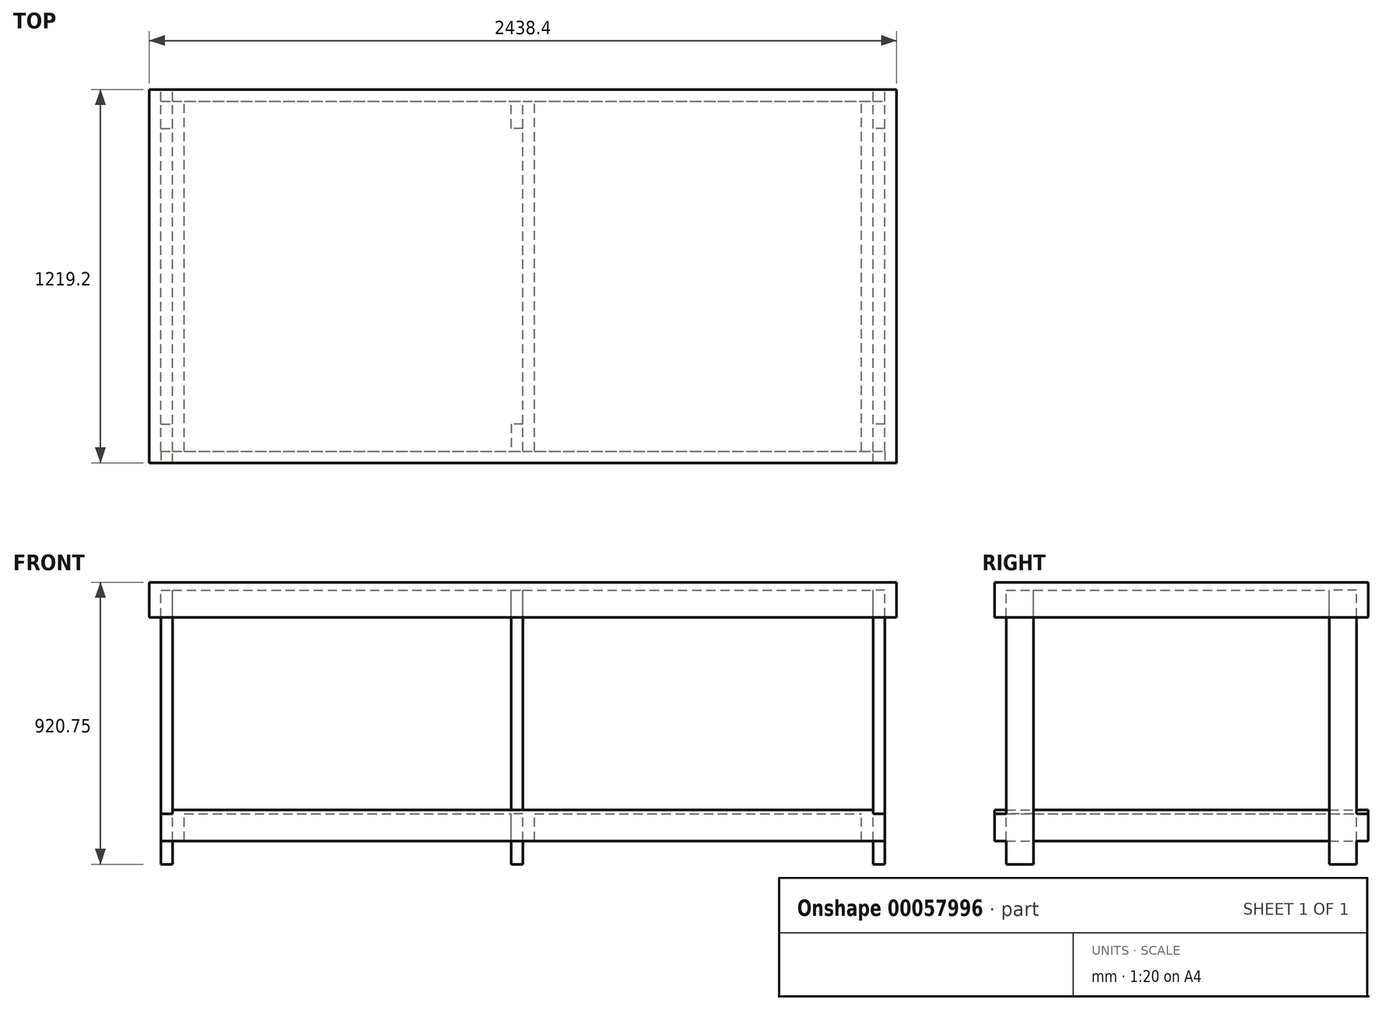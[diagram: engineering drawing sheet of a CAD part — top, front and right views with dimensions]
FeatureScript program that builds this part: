
annotation { "Feature Type Name" : "Feature", "Feature Type Description" : "" }
export const myFeature = defineFeature(function(context is Context, id is Id, definition is map)
    precondition{}
    {
        {
            var Q0;
            Q0=qCreatedBy(makeId("Top.planeOp"),FACE);
            var sketch = newSketch(context, id + "F0", { "sketchPlane" : qUnion([Q0])});
            skLineSegment(sketch, "E0.bottom", {"start": v(0, 0) * mm, "end": v(2438.4, 0) * mm});
            skLineSegment(sketch, "E0.top", {"start": v(0, -1219.2) * mm, "end": v(2438.4, -1219.2) * mm});
            skLineSegment(sketch, "E0.left", {"start": v(0, 0) * mm, "end": v(0, -1219.2) * mm});
            skLineSegment(sketch, "E0.right", {"start": v(2438.4, 0) * mm, "end": v(2438.4, -1219.2) * mm});
            skSolve(sketch);
        }
        {
            var Q0;
            Q0 = qSketchRegion(id + "F0", true);
            extrude(context, id + "F1", {"entities" : qUnion([Q0]), "depth" : 25.4 * mm});
        }
        {
            var Q0;
            Q0=makeQuery(id+"F1.opExtrude","CAP_FACE",FACE,{"disambiguationData":[OSD([sQuery(id+"F0.wireOp",EDGE,"E0.bottom"),sQuery(id+"F0.wireOp",EDGE,"E0.top"),sQuery(id+"F0.wireOp",EDGE,"E0.left"),sQuery(id+"F0.wireOp",EDGE,"E0.right")])],"isStart":true});
            var sketch = newSketch(context, id + "F2", { "sketchPlane" : qUnion([Q0])});
            skLineSegment(sketch, "E1.bottom", {"start": v(0, 1219.2) * mm, "end": v(2438.4, 1219.2) * mm});
            skLineSegment(sketch, "E1.top", {"start": v(0, 0) * mm, "end": v(2438.4, 0) * mm});
            skLineSegment(sketch, "E1.left", {"start": v(0, 1219.2) * mm, "end": v(0, 0) * mm});
            skLineSegment(sketch, "E1.right", {"start": v(2438.4, 1219.2) * mm, "end": v(2438.4, 0) * mm});
            skLineSegment(sketch, "E2.0", {"start": v(38.1, 1181.1) * mm, "end": v(2400.3, 1181.1) * mm});
            skLineSegment(sketch, "E2.1", {"start": v(38.1, 1181.1) * mm, "end": v(38.1, 38.1) * mm});
            skLineSegment(sketch, "E2.2", {"start": v(38.1, 38.1) * mm, "end": v(2400.3, 38.1) * mm});
            skLineSegment(sketch, "E2.3", {"start": v(2400.3, 1181.1) * mm, "end": v(2400.3, 38.1) * mm});
            skSolve(sketch);
        }
        {
            var Q0;
            Q0 = qSketchRegion(id + "F2", true);
            extrude(context, id + "F3", {"entities" : qUnion([Q0]), "operationType" : NewBodyOperationType.ADD, "depth" : 88.9 * mm});
        }
        {
            var Q0;
            Q0=makeQuery(id+"F1.opExtrude","CAP_FACE",FACE,{"disambiguationData":[OSD([sQuery(id+"F0.wireOp",EDGE,"E0.bottom"),sQuery(id+"F0.wireOp",EDGE,"E0.top"),sQuery(id+"F0.wireOp",EDGE,"E0.left"),sQuery(id+"F0.wireOp",EDGE,"E0.right")])],"isStart":true});
            var sketch = newSketch(context, id + "F4", { "sketchPlane" : qUnion([Q0])});
            skLineSegment(sketch, "E3.bottom", {"start": v(38.1, 1181.1) * mm, "end": v(76.2, 1181.1) * mm});
            skLineSegment(sketch, "E3.top", {"start": v(38.1, 1092.2) * mm, "end": v(76.2, 1092.2) * mm});
            skLineSegment(sketch, "E3.left", {"start": v(38.1, 1181.1) * mm, "end": v(38.1, 1092.2) * mm});
            skLineSegment(sketch, "E3.right", {"start": v(76.2, 1181.1) * mm, "end": v(76.2, 1092.2) * mm});
            skLineSegment(sketch, "E4.bottom", {"start": v(38.1, 38.1) * mm, "end": v(76.2, 38.1) * mm});
            skLineSegment(sketch, "E4.top", {"start": v(38.1, 127) * mm, "end": v(76.2, 127) * mm});
            skLineSegment(sketch, "E4.left", {"start": v(38.1, 38.1) * mm, "end": v(38.1, 127) * mm});
            skLineSegment(sketch, "E4.right", {"start": v(76.2, 38.1) * mm, "end": v(76.2, 127) * mm});
            skLineSegment(sketch, "E5.bottom", {"start": v(2400.3, 1181.1) * mm, "end": v(2362.2, 1181.1) * mm});
            skLineSegment(sketch, "E5.top", {"start": v(2400.3, 1092.2) * mm, "end": v(2362.2, 1092.2) * mm});
            skLineSegment(sketch, "E5.left", {"start": v(2400.3, 1181.1) * mm, "end": v(2400.3, 1092.2) * mm});
            skLineSegment(sketch, "E5.right", {"start": v(2362.2, 1181.1) * mm, "end": v(2362.2, 1092.2) * mm});
            skLineSegment(sketch, "E6.bottom", {"start": v(2400.3, 38.1) * mm, "end": v(2362.2, 38.1) * mm});
            skLineSegment(sketch, "E6.top", {"start": v(2400.3, 127) * mm, "end": v(2362.2, 127) * mm});
            skLineSegment(sketch, "E6.left", {"start": v(2400.3, 38.1) * mm, "end": v(2400.3, 127) * mm});
            skLineSegment(sketch, "E6.right", {"start": v(2362.2, 38.1) * mm, "end": v(2362.2, 127) * mm});
            skLineSegment(sketch, "E7.bottom", {"start": v(1181.1, 1181.1) * mm, "end": v(1219.2, 1181.1) * mm});
            skLineSegment(sketch, "E7.top", {"start": v(1181.1, 1092.2) * mm, "end": v(1219.2, 1092.2) * mm});
            skLineSegment(sketch, "E7.left", {"start": v(1181.1, 1181.1) * mm, "end": v(1181.1, 1092.2) * mm});
            skLineSegment(sketch, "E7.right", {"start": v(1219.2, 1181.1) * mm, "end": v(1219.2, 1092.2) * mm});
            skLineSegment(sketch, "E8.bottom", {"start": v(1181.1, 38.1) * mm, "end": v(1219.2, 38.1) * mm});
            skLineSegment(sketch, "E8.top", {"start": v(1181.1, 127) * mm, "end": v(1219.2, 127) * mm});
            skLineSegment(sketch, "E8.left", {"start": v(1181.1, 38.1) * mm, "end": v(1181.1, 127) * mm});
            skLineSegment(sketch, "E8.right", {"start": v(1219.2, 38.1) * mm, "end": v(1219.2, 127) * mm});
            skSolve(sketch);
        }
        {
            var Q0;
            Q0 = qSketchRegion(id + "F4", true);
            extrude(context, id + "F5", {"entities" : qUnion([Q0]), "operationType" : NewBodyOperationType.ADD, "depth" : 895.35 * mm});
        }
        {
            var Q0;
            Q0=qCreatedBy(makeId("Top.planeOp"),FACE);
            cPlane(context, id + "F6", {"entities" : qUnion([Q0]), "cplaneType" : CPlaneType.OFFSET, "offset" : 730.25 * mm, "oppositeDirection" : true, "width" : 152.4 * mm, "height" : 152.4 * mm});
        }
        {
            var Q0;
            Q0=qCreatedBy(id+"F6.planeOp",FACE);
            var sketch = newSketch(context, id + "F7", { "sketchPlane" : qUnion([Q0])});
            skLineSegment(sketch, "E9.bottom", {"start": v(38.1, 0) * mm, "end": v(2400.3, 0) * mm});
            skLineSegment(sketch, "E10.bottom", {"start": v(38.1, -1219.2) * mm, "end": v(2400.3, -1219.2) * mm});
            skLineSegment(sketch, "E10.top", {"start": v(38.1, -1181.1) * mm, "end": v(76.2, -1181.1) * mm});
            skLineSegment(sketch, "E11.right", {"start": v(2324.1, -1181.1) * mm, "end": v(2324.1, -38.1) * mm});
            skLineSegment(sketch, "E12.left", {"start": v(76.2, -1181.1) * mm, "end": v(76.2, -38.1) * mm});
            skLineSegment(sketch, "E12.right", {"start": v(114.3, -1181.1) * mm, "end": v(114.3, -38.1) * mm});
            skLineSegment(sketch, "E13.left", {"start": v(1219.2, -1181.1) * mm, "end": v(1219.2, -38.1) * mm});
            skLineSegment(sketch, "E13.right", {"start": v(1257.3, -1181.1) * mm, "end": v(1257.3, -38.1) * mm});
            skLineSegment(sketch, "E14.trimOffspring", {"start": v(114.3, -38.1) * mm, "end": v(1219.2, -38.1) * mm});
            skLineSegment(sketch, "E15.trimOffspring", {"start": v(114.3, -1181.1) * mm, "end": v(1219.2, -1181.1) * mm});
            skLineSegment(sketch, "E16.trimOffspring", {"start": v(1257.3, -1181.1) * mm, "end": v(2324.1, -1181.1) * mm});
            skLineSegment(sketch, "E17.trimOffspring", {"start": v(1257.3, -38.1) * mm, "end": v(2324.1, -38.1) * mm});
            skLineSegment(sketch, "E18.trimOffspring", {"start": v(2362.2, -38.1) * mm, "end": v(2400.3, -38.1) * mm});
            skLineSegment(sketch, "E19.trimOffspring", {"start": v(2362.2, -1181.1) * mm, "end": v(2400.3, -1181.1) * mm});
            skLineSegment(sketch, "E20", {"start": v(38.1, -1181.1) * mm, "end": v(38.1, -1219.2) * mm});
            skPoint(sketch, "E21.orphan", {"position": v(0, -1219.2) * mm});
            skPoint(sketch, "E22.orphan", {"position": v(0, -1181.1) * mm});
            skLineSegment(sketch, "E23", {"start": v(38.1, -38.1) * mm, "end": v(38.1, 0) * mm});
            skLineSegment(sketch, "E24", {"start": v(2400.3, -1181.1) * mm, "end": v(2400.3, -1219.2) * mm});
            skLineSegment(sketch, "E25", {"start": v(2400.3, -38.1) * mm, "end": v(2400.3, 0) * mm});
            skLineSegment(sketch, "E26", {"start": v(38.1, -38.1) * mm, "end": v(76.2, -38.1) * mm});
            skLineSegment(sketch, "E27", {"start": v(2362.2, -1181.1) * mm, "end": v(2362.2, -38.1) * mm});
            skSolve(sketch);
        }
        {
            var Q0;
            Q0 = qSketchRegion(id + "F7", true);
            extrude(context, id + "F8", {"entities" : qUnion([Q0]), "operationType" : NewBodyOperationType.ADD, "oppositeDirection" : true, "depth" : 88.9 * mm});
        }
        {
            var Q0;
            Q0=qCreatedBy(id+"F6.planeOp",FACE);
            var sketch = newSketch(context, id + "F9", { "sketchPlane" : qUnion([Q0])});
            skLineSegment(sketch, "E28.bottom", {"start": v(76.2, -1219.2) * mm, "end": v(2362.2, -1219.2) * mm});
            skLineSegment(sketch, "E28.top", {"start": v(76.2, 0) * mm, "end": v(2362.2, 0) * mm});
            skLineSegment(sketch, "E28.left", {"start": v(76.2, -1219.2) * mm, "end": v(76.2, 0) * mm});
            skLineSegment(sketch, "E28.right", {"start": v(2362.2, -1219.2) * mm, "end": v(2362.2, 0) * mm});
            skSolve(sketch);
        }
        {
            var Q0;
            Q0 = qSketchRegion(id + "F9", true);
            extrude(context, id + "F10", {"entities" : qUnion([Q0]), "operationType" : NewBodyOperationType.ADD, "depth" : 12.7 * mm});
        }
    });
